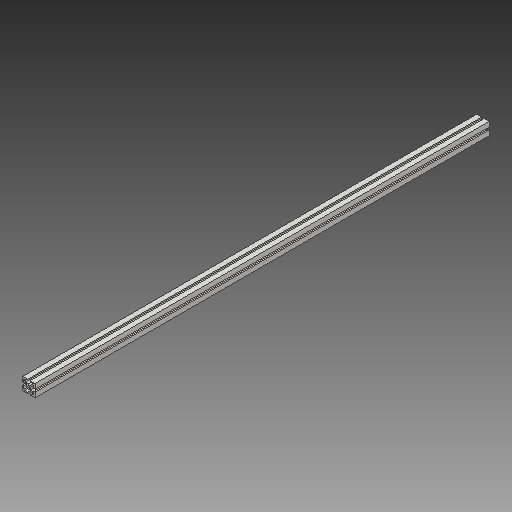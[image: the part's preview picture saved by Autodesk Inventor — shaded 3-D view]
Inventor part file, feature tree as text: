
AUTODESK INVENTOR PART (.ipt)
format: ipt  version: 2018 (Build 220112000, 112)  size: 141,824 bytes
history: native  units: mm
features: extrude x1, sketch x1
ambient origin geometry x8: Origin, YZ Plane, XZ Plane, XY Plane, X Axis, Y Axis, Z Axis, Center Point
bodies: Volumenkörper1 (feature_tree)
feature tree (2):
  extrude  "Extrusion1"  Depth=3.0mm
  sketch  "Skizze1"  dims[d0=3.0mm d1=3.0mm d2=0.5mm d3=1.0mm d4=1.0mm d5=1.2mm d6=1.2mm d7=1.2mm d8=1.2mm d9=0.3mm d10=0.15mm d11=0.15mm d12=0.15mm d13=0.15mm d14=110.0mm d15=0.0mm]
